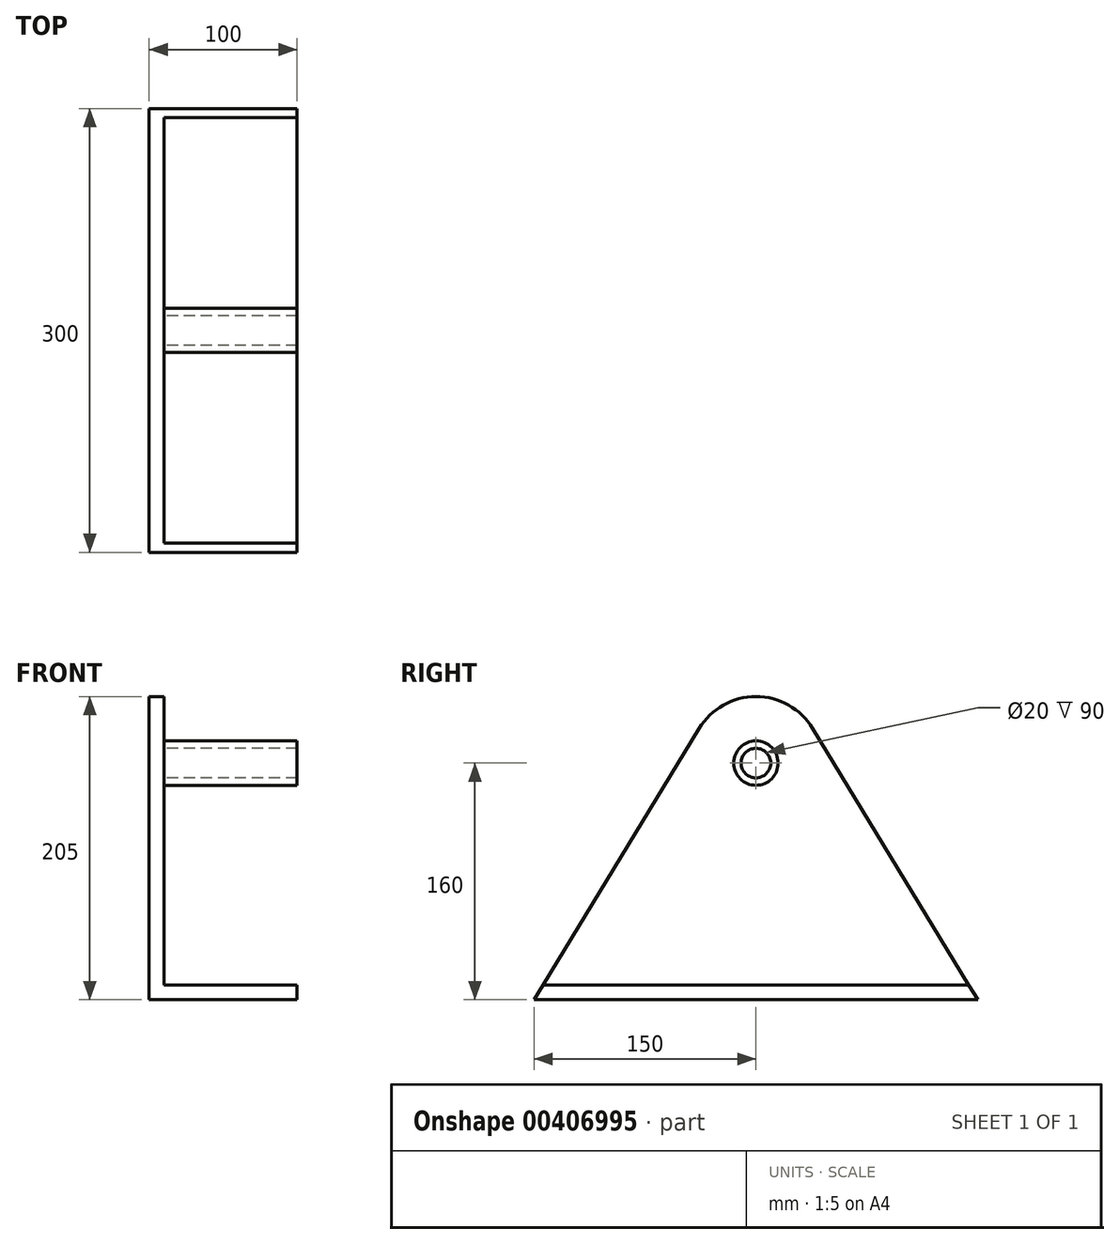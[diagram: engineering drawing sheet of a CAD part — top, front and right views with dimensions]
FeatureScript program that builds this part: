
annotation { "Feature Type Name" : "Feature", "Feature Type Description" : "" }
export const myFeature = defineFeature(function(context is Context, id is Id, definition is map)
    precondition{}
    {
        {
            var Q0;
            Q0=qCreatedBy(makeId("Right.planeOp"),FACE);
            var sketch = newSketch(context, id + "F0", { "sketchPlane" : qUnion([Q0])});
            skLineSegment(sketch, "E0", {"start": v(0, 0) * mm, "end": v(-150, 0) * mm});
            skLineSegment(sketch, "E1", {"start": v(-150, 0) * mm, "end": v(-38.45, 183.39) * mm});
            skLineSegment(sketch, "E2", {"start": v(-52.67, 160) * mm, "end": v(0, 160) * mm, "construction": true});
            skLineSegment(sketch, "E3", {"start": v(38.45, 183.39) * mm, "end": v(150, 0) * mm});
            skLineSegment(sketch, "E4", {"start": v(150, 0) * mm, "end": v(0, 0) * mm});
            skLineSegment(sketch, "E5", {"start": v(0, 160) * mm, "end": v(52.67, 160) * mm, "construction": true});
            skCircle(sketch, "E6", {"center": v(0, 160) * mm, "radius": 15 * mm});
            skCircle(sketch, "E7", {"center": v(0, 160) * mm, "radius": 45 * mm});
            skCircle(sketch, "E8", {"center": v(0, 160) * mm, "radius": 10 * mm});
            skCircle(sketch, "E9", {"center": v(0, 160) * mm, "radius": 8 * mm});
            skLineSegment(sketch, "E10", {"start": v(0, 10) * mm, "end": v(-143.92, 10) * mm});
            skLineSegment(sketch, "E11", {"start": v(0, 10) * mm, "end": v(143.92, 10) * mm});
            skSolve(sketch);
        }
        {
            var Q0;
            Q0 = qSketchRegion(id + "F0", true);
            extrude(context, id + "F1", {"entities" : qUnion([Q0]), "depth" : 10 * mm});
        }
        {
            var Q0;
            Q0=makeQuery(id+"F0.imprint","IMPRINT",FACE,{"disambiguationData":[TD([[makeQuery(id+"F0.imprint","IMPRINT",EDGE,{"derivedFrom":sQuery(id+"F0.wireOp",EDGE,"E6")}),1.0]])]});
            extrude(context, id + "F2", {"entities" : qUnion([Q0]), "operationType" : NewBodyOperationType.ADD, "depth" : 100 * mm});
        }
        {
            var Q0;
            Q0=makeQuery(id+"F0.imprint","IMPRINT",FACE,{"disambiguationData":[TD([[makeQuery(id+"F0.imprint","IMPRINT",EDGE,{"derivedFrom":sQuery(id+"F0.wireOp",EDGE,"E8")}),1.0]])]});
            extrude(context, id + "F3", {"entities" : qUnion([Q0]), "operationType" : NewBodyOperationType.ADD, "depth" : 10 * mm});
        }
        {
            var Q0;
            Q0=makeQuery(id+"F0.imprint","IMPRINT",FACE,{"disambiguationData":[TD([[makeQuery(id+"F0.imprint","IMPRINT",EDGE,{"derivedFrom":sQuery(id+"F0.wireOp",EDGE,"E9")}),1.0]])]});
            extrude(context, id + "F4", {"entities" : qUnion([Q0]), "operationType" : NewBodyOperationType.ADD, "depth" : 10 * mm});
        }
        {
            var Q0;
            {var subQ4=sQuery(id+"F0.wireOp",EDGE,"E0");Q0=makeQuery(id+"F0.imprint","IMPRINT",FACE,{"disambiguationData":[TD([[makeQuery(id+"F0.imprint","IMPRINT",EDGE,{"derivedFrom":subQ4}),-1.0]])]});}
            extrude(context, id + "F5", {"entities" : qUnion([Q0]), "operationType" : NewBodyOperationType.ADD, "depth" : 100 * mm});
        }
    });
